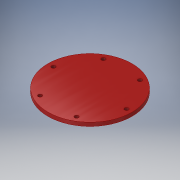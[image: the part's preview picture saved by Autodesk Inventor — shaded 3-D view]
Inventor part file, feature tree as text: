
AUTODESK INVENTOR PART (.ipt)
format: ipt  version: 2019.1 (Build 231200000, 200)  size: 119,296 bytes
history: native  units: in
note: dims shown in document units (in); Inventor stores cm internally (conversion verified against a paired STEP export)
features: extrude x2, sketch x2
ambient origin geometry x8: Origin, YZ Plane, XZ Plane, XY Plane, X Axis, Y Axis, Z Axis, Center Point
bodies: Solid1 (feature_tree)
feature tree (4):
  extrude  "Extrusion1"  Depth=0.25in
  extrude  "Extrusion5"  Depth=2.5in
  sketch  "Sketch1"  dims[d0=0.25in d1=0.0in d4=5.75in]
  sketch  "Sketch7"  dims[d32=0.266in d33=2.5in d34=2.3622in d36=360.0deg d38=1.0in d39=0.0in]
